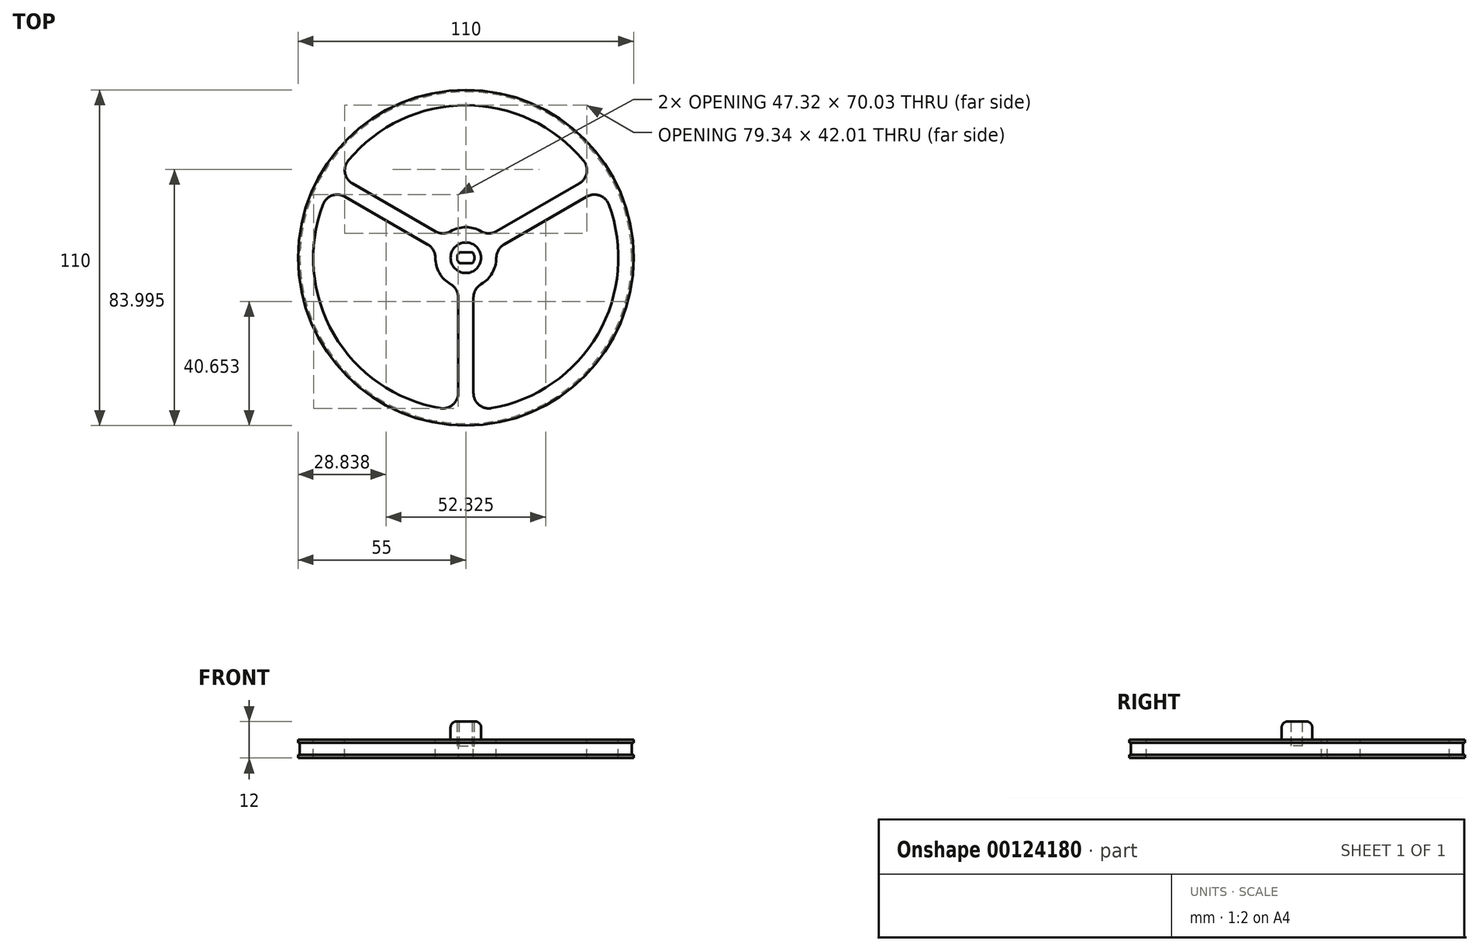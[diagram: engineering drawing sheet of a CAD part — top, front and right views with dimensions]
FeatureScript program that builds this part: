
annotation { "Feature Type Name" : "Feature", "Feature Type Description" : "" }
export const myFeature = defineFeature(function(context is Context, id is Id, definition is map)
    precondition{}
    {
        {
            var Q0;
            Q0=qCreatedBy(makeId("Top.planeOp"),FACE);
            var sketch = newSketch(context, id + "F0", { "sketchPlane" : qUnion([Q0])});
            skCircle(sketch, "E0", {"center": v(0, 0) * mm, "radius": 55 * mm});
            skSolve(sketch);
        }
        {
            var Q0;
            Q0 = qSketchRegion(id + "F0", true);
            extrude(context, id + "F1", {"entities" : qUnion([Q0]), "depth" : 6 * mm});
        }
        {
            var Q0;
            Q0=makeQuery(id+"F1.opExtrude","CAP_FACE",FACE,{"disambiguationData":[OSD([sQuery(id+"F0.wireOp",EDGE,"E0")])],"isStart":false});
            var sketch = newSketch(context, id + "F2", { "sketchPlane" : qUnion([Q0])});
            skCircle(sketch, "E1", {"center": v(0, 0) * mm, "radius": 5 * mm});
            skSolve(sketch);
        }
        {
            var Q0;
            Q0 = qSketchRegion(id + "F2", true);
            extrude(context, id + "F3", {"entities" : qUnion([Q0]), "operationType" : NewBodyOperationType.ADD, "depth" : 6 * mm});
        }
        {
            var Q0;
            Q0=makeQuery(id+"F3.opExtrude","CAP_FACE",FACE,{"disambiguationData":[OSD([sQuery(id+"F2.wireOp",EDGE,"E1")])],"isStart":false});
            var sketch = newSketch(context, id + "F4", { "sketchPlane" : qUnion([Q0])});
            skArc(sketch, "E2", {"start": v(-2.15, 1.82) * mm, "mid": v(-2.82, 0) * mm, "end": v(-2.15, -1.83) * mm});
            skLineSegment(sketch, "E3.bottom", {"start": v(-2.15, 1.83) * mm, "end": v(2.15, 1.83) * mm});
            skLineSegment(sketch, "E3.top", {"start": v(-2.15, -1.83) * mm, "end": v(2.15, -1.83) * mm});
            skArc(sketch, "E4.trimOffspring", {"start": v(2.15, -1.82) * mm, "mid": v(2.82, 0) * mm, "end": v(2.15, 1.83) * mm});
            skSolve(sketch);
        }
        {
            var Q0;
            Q0 = qSketchRegion(id + "F4", true);
            extrude(context, id + "F5", {"entities" : qUnion([Q0]), "operationType" : NewBodyOperationType.REMOVE, "oppositeDirection" : true, "depth" : 8 * mm});
        }
        {
            var Q0;
            Q0=qCreatedBy(makeId("Top.planeOp"),FACE);
            cPlane(context, id + "F6", {"entities" : qUnion([Q0]), "cplaneType" : CPlaneType.OFFSET, "offset" : 1 * mm, "width" : 150 * mm, "height" : 150 * mm});
        }
        {
            var Q0;
            Q0=qCreatedBy(id+"F6.planeOp",FACE);
            var sketch = newSketch(context, id + "F7", { "sketchPlane" : qUnion([Q0])});
            skCircle(sketch, "E5.0", {"center": v(0, 0) * mm, "radius": 55 * mm});
            skCircle(sketch, "E6.0", {"center": v(0, 0) * mm, "radius": 54.4 * mm});
            skSolve(sketch);
        }
        {
            var Q0;
            Q0 = qSketchRegion(id + "F7", true);
            extrude(context, id + "F8", {"entities" : qUnion([Q0]), "operationType" : NewBodyOperationType.REMOVE, "depth" : 4 * mm});
        }
        {
            var Q0;
            Q0=makeQuery(id+"F1.opExtrude","CAP_FACE",FACE,{"disambiguationData":[OSD([sQuery(id+"F0.wireOp",EDGE,"E0")])],"isStart":false});
            var sketch = newSketch(context, id + "F9", { "sketchPlane" : qUnion([Q0])});
            skCircle(sketch, "E7.0", {"center": v(0, 0) * mm, "radius": 50 * mm});
            skCircle(sketch, "E8.0", {"center": v(0, 0) * mm, "radius": 10 * mm});
            skLineSegment(sketch, "E9", {"start": v(0, -10) * mm, "end": v(0, -50) * mm, "construction": true});
            skLineSegment(sketch, "E10.bottom", {"start": v(-2.5, -9.68) * mm, "end": v(2.5, -9.68) * mm});
            skLineSegment(sketch, "E10.top", {"start": v(-2.5, -50.32) * mm, "end": v(2.5, -50.32) * mm});
            skLineSegment(sketch, "E10.left", {"start": v(-2.5, -9.68) * mm, "end": v(-2.5, -50.32) * mm});
            skLineSegment(sketch, "E10.right", {"start": v(2.5, -9.68) * mm, "end": v(2.5, -50.32) * mm});
            skPoint(sketch, "E10.middle", {"position": v(0, -30) * mm});
            skLineSegment(sketch, "E11.1.0", {"start": v(7.14, 7) * mm, "end": v(42.33, 27.32) * mm});
            skLineSegment(sketch, "E11.1.1", {"start": v(9.64, 2.68) * mm, "end": v(44.83, 23) * mm});
            skLineSegment(sketch, "E11.2.0", {"start": v(-9.64, 2.68) * mm, "end": v(-44.83, 23) * mm});
            skLineSegment(sketch, "E11.2.1", {"start": v(-7.14, 7) * mm, "end": v(-42.33, 27.32) * mm});
            skSolve(sketch);
        }
        {
            var Q0;
            {var subQ0=sQuery(id+"F9.wireOp",EDGE,"E11.1.0");var subQ1=sQuery(id+"F9.wireOp",EDGE,"E7.0");var subQ2=makeQuery(id+"F9.imprint","INTERSECT",VERTEX,{"derivedFrom":[subQ1,subQ0]});Q0=makeQuery(id+"F9.imprint","IMPRINT",FACE,{"disambiguationData":[TD([[makeQuery(id+"F9.imprint","IMPRINT",EDGE,{"disambiguationData":[TD([[subQ2,-1.0]])],"derivedFrom":subQ1}),1.0]])]});}
            var Q1;
            {var subQ0=sQuery(id+"F9.wireOp",EDGE,"E11.1.1");var subQ1=sQuery(id+"F9.wireOp",EDGE,"E7.0");var subQ2=makeQuery(id+"F9.imprint","INTERSECT",VERTEX,{"derivedFrom":[subQ1,subQ0]});Q1=makeQuery(id+"F9.imprint","IMPRINT",FACE,{"disambiguationData":[TD([[makeQuery(id+"F9.imprint","IMPRINT",EDGE,{"disambiguationData":[TD([[subQ2,1.0]])],"derivedFrom":subQ1}),1.0]])]});}
            var Q2;
            {var subQ0=sQuery(id+"F9.wireOp",EDGE,"E11.2.0");var subQ1=sQuery(id+"F9.wireOp",EDGE,"E7.0");var subQ2=makeQuery(id+"F9.imprint","INTERSECT",VERTEX,{"derivedFrom":[subQ1,subQ0]});Q2=makeQuery(id+"F9.imprint","IMPRINT",FACE,{"disambiguationData":[TD([[makeQuery(id+"F9.imprint","IMPRINT",EDGE,{"disambiguationData":[TD([[subQ2,-1.0]])],"derivedFrom":subQ1}),1.0]])]});}
            extrude(context, id + "F10", {"entities" : qUnion([Q0, Q1, Q2]), "operationType" : NewBodyOperationType.REMOVE, "oppositeDirection" : true, "depth" : 25 * mm});
        }
        {
            var Q0;
            Q0=makeQuery(id+"F10.boolean.opBoolean","COPY",EDGE,{"derivedFrom":makeQuery(id+"F10.opExtrude","SWEPT_EDGE",EDGE,{"disambiguationData":[OSD([sQuery(id+"F9.wireOp",EDGE,"E7.0"),sQuery(id+"F9.wireOp",EDGE,"E11.2.0")])]})});
            var Q1;
            Q1=makeQuery(id+"F10.boolean.opBoolean","COPY",EDGE,{"derivedFrom":makeQuery(id+"F10.opExtrude","SWEPT_EDGE",EDGE,{"disambiguationData":[OSD([sQuery(id+"F9.wireOp",EDGE,"E7.0"),sQuery(id+"F9.wireOp",EDGE,"E11.2.1")])]})});
            var Q2;
            Q2=makeQuery(id+"F10.boolean.opBoolean","COPY",EDGE,{"derivedFrom":makeQuery(id+"F10.opExtrude","SWEPT_EDGE",EDGE,{"disambiguationData":[OSD([sQuery(id+"F9.wireOp",EDGE,"E7.0"),sQuery(id+"F9.wireOp",EDGE,"E11.1.0")])]})});
            var Q3;
            Q3=makeQuery(id+"F10.boolean.opBoolean","COPY",EDGE,{"derivedFrom":makeQuery(id+"F10.opExtrude","SWEPT_EDGE",EDGE,{"disambiguationData":[OSD([sQuery(id+"F9.wireOp",EDGE,"E7.0"),sQuery(id+"F9.wireOp",EDGE,"E11.1.1")])]})});
            var Q4;
            Q4=makeQuery(id+"F10.boolean.opBoolean","COPY",EDGE,{"derivedFrom":makeQuery(id+"F10.opExtrude","SWEPT_EDGE",EDGE,{"disambiguationData":[OSD([sQuery(id+"F9.wireOp",EDGE,"E7.0"),sQuery(id+"F9.wireOp",EDGE,"E10.right")])]})});
            var Q5;
            Q5=makeQuery(id+"F10.boolean.opBoolean","COPY",EDGE,{"derivedFrom":makeQuery(id+"F10.opExtrude","SWEPT_EDGE",EDGE,{"disambiguationData":[OSD([sQuery(id+"F9.wireOp",EDGE,"E7.0"),sQuery(id+"F9.wireOp",EDGE,"E10.left")])]})});
            fillet(context, id + "F11", {"entities" : qUnion([Q0, Q1, Q2, Q3, Q4, Q5]), "radius" : 5 * mm, "tangentPropagation" : true, "allowEdgeOverflow" : false});
        }
        {
            var Q0;
            Q0=makeQuery(id+"F10.boolean.opBoolean","COPY",EDGE,{"derivedFrom":makeQuery(id+"F10.opExtrude","SWEPT_EDGE",EDGE,{"disambiguationData":[OSD([sQuery(id+"F9.wireOp",EDGE,"E8.0"),sQuery(id+"F9.wireOp",EDGE,"E11.2.0")])]})});
            var Q1;
            Q1=makeQuery(id+"F10.boolean.opBoolean","COPY",EDGE,{"derivedFrom":makeQuery(id+"F10.opExtrude","SWEPT_EDGE",EDGE,{"disambiguationData":[OSD([sQuery(id+"F9.wireOp",EDGE,"E8.0"),sQuery(id+"F9.wireOp",EDGE,"E10.bottom"),sQuery(id+"F9.wireOp",EDGE,"E10.left")])]})});
            var Q2;
            Q2=makeQuery(id+"F10.boolean.opBoolean","COPY",EDGE,{"derivedFrom":makeQuery(id+"F10.opExtrude","SWEPT_EDGE",EDGE,{"disambiguationData":[OSD([sQuery(id+"F9.wireOp",EDGE,"E8.0"),sQuery(id+"F9.wireOp",EDGE,"E10.bottom"),sQuery(id+"F9.wireOp",EDGE,"E10.right")])]})});
            var Q3;
            Q3=makeQuery(id+"F10.boolean.opBoolean","COPY",EDGE,{"derivedFrom":makeQuery(id+"F10.opExtrude","SWEPT_EDGE",EDGE,{"disambiguationData":[OSD([sQuery(id+"F9.wireOp",EDGE,"E8.0"),sQuery(id+"F9.wireOp",EDGE,"E11.1.1")])]})});
            var Q4;
            Q4=makeQuery(id+"F10.boolean.opBoolean","COPY",EDGE,{"derivedFrom":makeQuery(id+"F10.opExtrude","SWEPT_EDGE",EDGE,{"disambiguationData":[OSD([sQuery(id+"F9.wireOp",EDGE,"E8.0"),sQuery(id+"F9.wireOp",EDGE,"E11.1.0")])]})});
            var Q5;
            Q5=makeQuery(id+"F10.boolean.opBoolean","COPY",EDGE,{"derivedFrom":makeQuery(id+"F10.opExtrude","SWEPT_EDGE",EDGE,{"disambiguationData":[OSD([sQuery(id+"F9.wireOp",EDGE,"E8.0"),sQuery(id+"F9.wireOp",EDGE,"E11.2.1")])]})});
            fillet(context, id + "F12", {"entities" : qUnion([Q0, Q1, Q2, Q3, Q4, Q5]), "radius" : 5 * mm, "tangentPropagation" : true, "allowEdgeOverflow" : false});
        }
        {
            var Q0;
            Q0=makeQuery(id+"F3.opExtrude","CAP_EDGE",EDGE,{"disambiguationData":[OSD([sQuery(id+"F2.wireOp",EDGE,"E1")])],"isStart":true});
            var Q1;
            Q1=makeQuery(id+"F3.opExtrude","CAP_EDGE",EDGE,{"disambiguationData":[OSD([sQuery(id+"F2.wireOp",EDGE,"E1")])],"isStart":false});
            fillet(context, id + "F13", {"entities" : qUnion([Q0, Q1]), "radius" : 2 * mm, "tangentPropagation" : true, "allowEdgeOverflow" : false});
        }
    });
